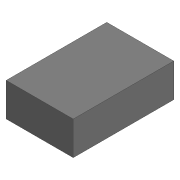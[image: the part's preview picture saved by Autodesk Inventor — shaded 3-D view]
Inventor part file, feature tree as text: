
AUTODESK INVENTOR PART (.ipt)
format: ipt  version: 2020.3 (Build 243373000, 373)  size: 74,240 bytes
history: native  units: mm
features: extrude x1, sketch x1
ambient origin geometry x8: Origin, YZ Plane, XZ Plane, XY Plane, X Axis, Y Axis, Z Axis, Center Point
bodies: Solid1 (feature_tree)
feature tree (2):
  extrude  "Extrusion1"  Depth=60.0mm
  sketch  "Sketch1"  dims[d0=40.0mm d1=60.0mm d2=20.0mm d3=0.0mm]
